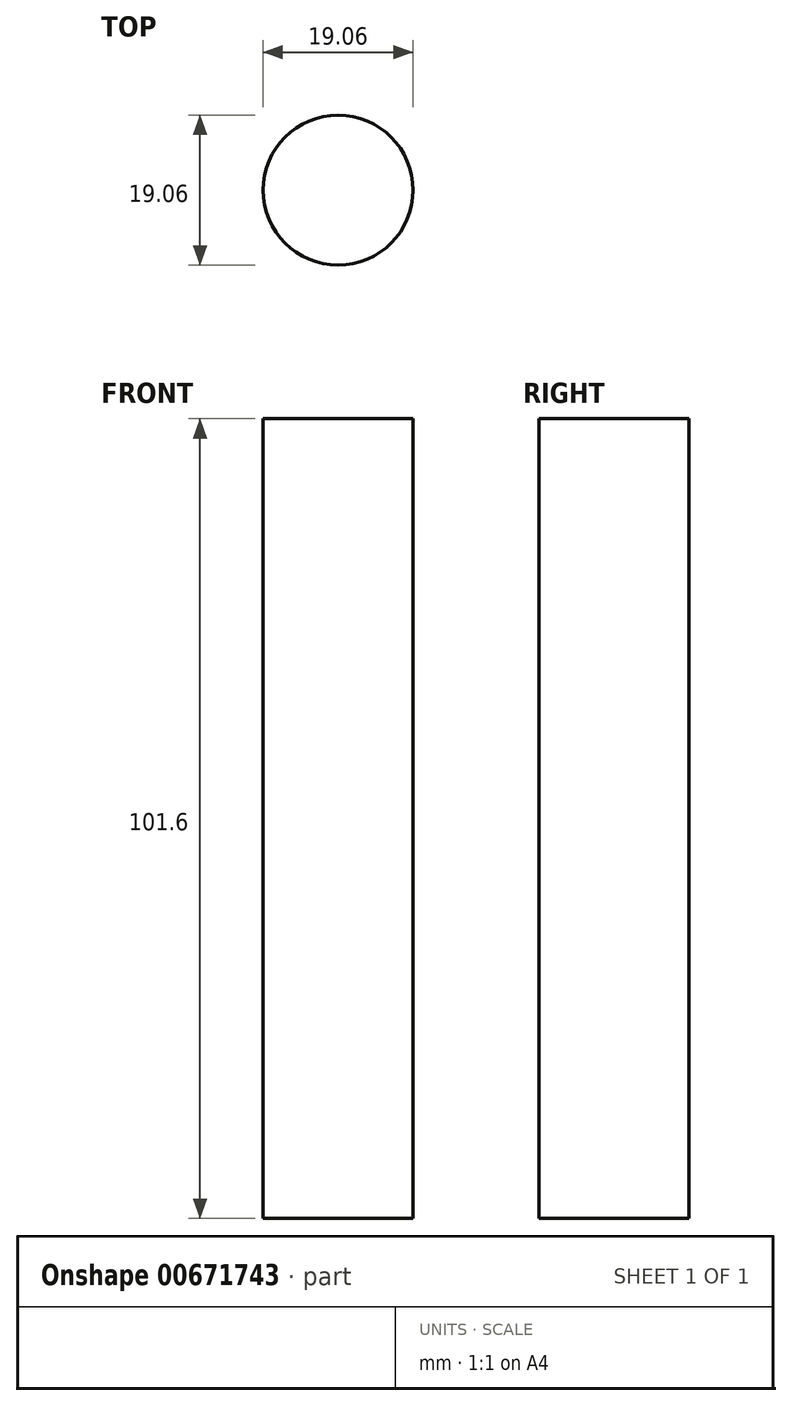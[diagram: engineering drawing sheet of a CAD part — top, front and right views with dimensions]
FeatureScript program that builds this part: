
annotation { "Feature Type Name" : "Feature", "Feature Type Description" : "" }
export const myFeature = defineFeature(function(context is Context, id is Id, definition is map)
    precondition{}
    {
        {
            var Q0;
            Q0=qCreatedBy(makeId("Top.planeOp"),FACE);
            var sketch = newSketch(context, id + "F0", { "sketchPlane" : qUnion([Q0])});
            skCircle(sketch, "E0", {"center": v(0, 0) * mm, "radius": 9.53 * mm});
            skSolve(sketch);
        }
        {
            var Q0;
            Q0 = qSketchRegion(id + "F0", true);
            extrude(context, id + "F1", {"entities" : qUnion([Q0]), "depth" : 101.6 * mm, "offsetDistance" : 25.4 * mm});
        }
    });
